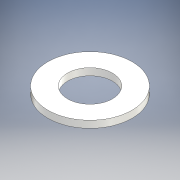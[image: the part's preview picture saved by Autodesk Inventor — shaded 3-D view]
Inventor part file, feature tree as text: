
AUTODESK INVENTOR PART (.ipt)
format: ipt  version: 2020.2 (Build 242310000, 310)  size: 103,936 bytes
history: native  units: mm
features: other x1, extrude x1, sketch x1
ambient origin geometry x8: Origin, YZ Plane, XZ Plane, XY Plane, X Axis, Y Axis, Z Axis, Center Point
bodies: Body1 (feature_tree)
feature tree (3):
  other  "ソリッド1"
  extrude  "押し出し1"  Depth=3.2mm
  sketch  "スケッチ1"
